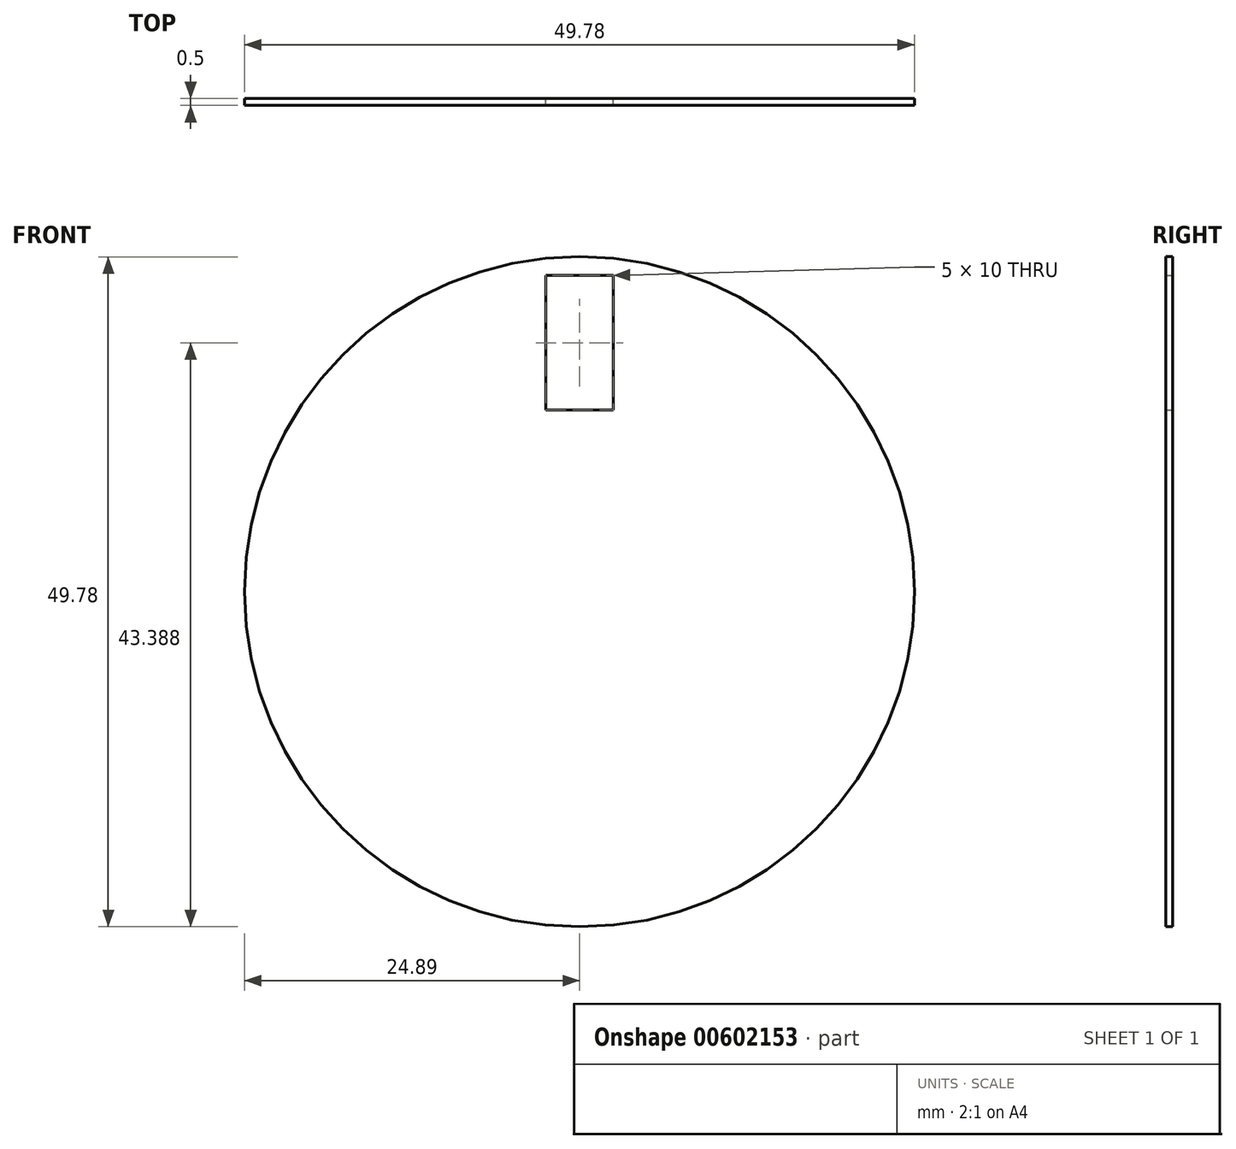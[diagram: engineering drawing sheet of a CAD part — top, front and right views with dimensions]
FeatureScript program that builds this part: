
annotation { "Feature Type Name" : "Feature", "Feature Type Description" : "" }
export const myFeature = defineFeature(function(context is Context, id is Id, definition is map)
    precondition{}
    {
        {
            var Q0;
            Q0=qCreatedBy(makeId("Front.planeOp"),FACE);
            var sketch = newSketch(context, id + "F0", { "sketchPlane" : qUnion([Q0])});
            skCircle(sketch, "E0", {"center": v(0, 0) * mm, "radius": 26.67 * mm});
            skSolve(sketch);
        }
        {
            var Q0;
            Q0=qCreatedBy(makeId("Front.planeOp"),FACE);
            var sketch = newSketch(context, id + "F1", { "sketchPlane" : qUnion([Q0])});
            skLineSegment(sketch, "E1.bottom", {"start": v(2.5, 13.5) * mm, "end": v(-2.5, 13.5) * mm});
            skLineSegment(sketch, "E1.top", {"start": v(2.5, 23.5) * mm, "end": v(-2.5, 23.5) * mm});
            skLineSegment(sketch, "E1.left", {"start": v(2.5, 13.5) * mm, "end": v(2.5, 23.5) * mm});
            skLineSegment(sketch, "E1.right", {"start": v(-2.5, 13.5) * mm, "end": v(-2.5, 23.5) * mm});
            skPoint(sketch, "E1.middle", {"position": v(0, 18.5) * mm});
            skSolve(sketch);
        }
        {
            var Q0;
            Q0=qCreatedBy(makeId("Front.planeOp"),FACE);
            var sketch = newSketch(context, id + "F2", { "sketchPlane" : qUnion([Q0])});
            skCircle(sketch, "E2", {"center": v(0, 0) * mm, "radius": 24.9 * mm});
            skSolve(sketch);
        }
        {
            var Q0;
            Q0 = qSketchRegion(id + "F2", true);
            var Q1;
            Q1 = qConstructionFilter(qBodyType(qCreatedBy(id + "F0" ,EDGE), BodyType.WIRE), ConstructionObject.NO);
            extrude(context, id + "F3", {"entities" : qUnion([Q0]), "bodyType" : ToolBodyType.SURFACE, "surfaceEntities" : qUnion([Q1]), "depth" : 1 * mm, "offsetDistance" : 25.4 * mm});
        }
        {
            var Q0;
            Q0 = qSketchRegion(id + "F2", true);
            var Q1;
            Q1 = qConstructionFilter(qBodyType(qCreatedBy(id + "F2" ,EDGE), BodyType.WIRE), ConstructionObject.NO);
            extrude(context, id + "F4", {"entities" : qUnion([Q0]), "bodyType" : ToolBodyType.SURFACE, "surfaceEntities" : qUnion([Q1]), "depth" : 6 * mm, "offsetDistance" : 25.4 * mm});
        }
        {
            var Q0;
            Q0=makeQuery(id+"F2.imprint","IMPRINT",FACE,{"disambiguationData":[TD([[makeQuery(id+"F2.imprint","IMPRINT",EDGE,{"derivedFrom":sQuery(id+"F2.wireOp",EDGE,"E2")}),1.0]])]});
            extrude(context, id + "F5", {"entities" : qUnion([Q0]), "depth" : 0.5 * mm, "offsetDistance" : 25.4 * mm});
        }
        {
            var Q0;
            Q0 = qSketchRegion(id + "F1", true);
            extrude(context, id + "F6", {"entities" : qUnion([Q0]), "operationType" : NewBodyOperationType.REMOVE, "depth" : 2.62 * mm, "offsetDistance" : 25.4 * mm});
        }
    });
